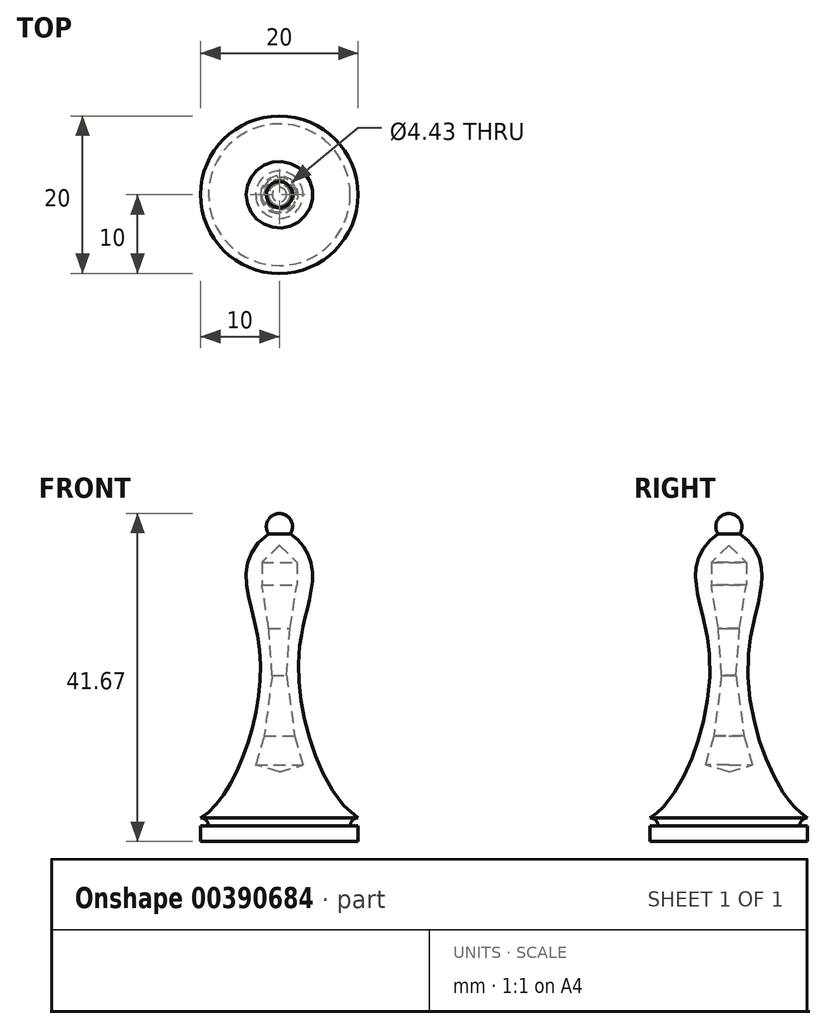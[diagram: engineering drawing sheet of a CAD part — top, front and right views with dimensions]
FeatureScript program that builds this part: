
annotation { "Feature Type Name" : "Feature", "Feature Type Description" : "" }
export const myFeature = defineFeature(function(context is Context, id is Id, definition is map)
    precondition{}
    {
        {
            var Q0;
            Q0=qCreatedBy(makeId("Front.planeOp"),FACE);
            var sketch = newSketch(context, id + "F0", { "sketchPlane" : qUnion([Q0])});
            skLineSegment(sketch, "E0", {"start": v(0, 0) * mm, "end": v(10, 0) * mm});
            skLineSegment(sketch, "E1", {"start": v(10, 0) * mm, "end": v(10, 2) * mm});
            skLineSegment(sketch, "E2", {"start": v(10, 2) * mm, "end": v(9, 2) * mm});
            skPoint(sketch, "E3.endSnap0", {"position": v(10, 1) * mm});
            skArc(sketch, "E4", {"start": v(9, 2) * mm, "mid": v(9.3, 2.7) * mm, "end": v(10, 3) * mm});
            skFitSpline(sketch, "E5", {"points": [v(10, 3) * mm, v(2.5, 24.16) * mm, v(0, 40) * mm], "startDerivative": vector(-23.82, 13.93) * mm, "endDerivative": vector(-47.1, 26.64) * mm});
            skLineSegment(sketch, "E6", {"start": v(0, 0) * mm, "end": v(0, 40) * mm});
            skArc(sketch, "E7", {"start": v(0, 38.33) * mm, "mid": v(1.67, 40) * mm, "end": v(0, 41.67) * mm});
            skLineSegment(sketch, "E8", {"start": v(0, 40) * mm, "end": v(0, 41.67) * mm});
            skLineSegment(sketch, "E9", {"start": v(0, 37.62) * mm, "end": v(2.21, 35.46) * mm});
            skLineSegment(sketch, "E10", {"start": v(2.21, 35.46) * mm, "end": v(2.21, 32.58) * mm});
            skLineSegment(sketch, "E11", {"start": v(2.21, 32.58) * mm, "end": v(1.35, 27.1) * mm});
            skLineSegment(sketch, "E12", {"start": v(1.35, 27.1) * mm, "end": v(0.92, 21.11) * mm});
            skLineSegment(sketch, "E13", {"start": v(0.92, 21.11) * mm, "end": v(1.93, 13.4) * mm});
            skLineSegment(sketch, "E14", {"start": v(1.93, 13.4) * mm, "end": v(3, 9.72) * mm});
            skLineSegment(sketch, "E15", {"start": v(3, 9.72) * mm, "end": v(0, 8.84) * mm});
            skSolve(sketch);
        }
        {
            var Q0;
            {var subQ0=sQuery(id+"F0.wireOp",EDGE,"E0");Q0=makeQuery(id+"F0.imprint","IMPRINT",FACE,{"disambiguationData":[TD([[makeQuery(id+"F0.imprint","IMPRINT",EDGE,{"derivedFrom":subQ0}),1.0]])]});}
            var Q1;
            {var subQ0=sQuery(id+"F0.wireOp",EDGE,"E8");Q1=makeQuery(id+"F0.imprint","IMPRINT",FACE,{"disambiguationData":[TD([[makeQuery(id+"F0.imprint","IMPRINT",EDGE,{"derivedFrom":subQ0}),-1.0]])]});}
            var Q2;
            {var subQ0=sQuery(id+"F0.wireOp",EDGE,"E6");var subQ3=sQuery(id+"F0.wireOp",EDGE,"E7");var subQ5=makeQuery(id+"F0.imprint","INTERSECT",VERTEX,{"derivedFrom":[subQ0,subQ3]});Q2=makeQuery(id+"F0.imprint","IMPRINT",FACE,{"disambiguationData":[TD([[makeQuery(id+"F0.imprint","IMPRINT",EDGE,{"disambiguationData":[TD([[subQ5,-1.0]])],"derivedFrom":subQ3}),1.0]])]});}
            var Q3;
            Q3=sQuery(id+"F0.wireOp",EDGE,"E6");
            revolve(context, id + "F1", {"entities" : qUnion([Q0, Q1, Q2]), "axis" : qUnion([Q3]), "revolveType" : RevolveType.FULL});
        }
    });
